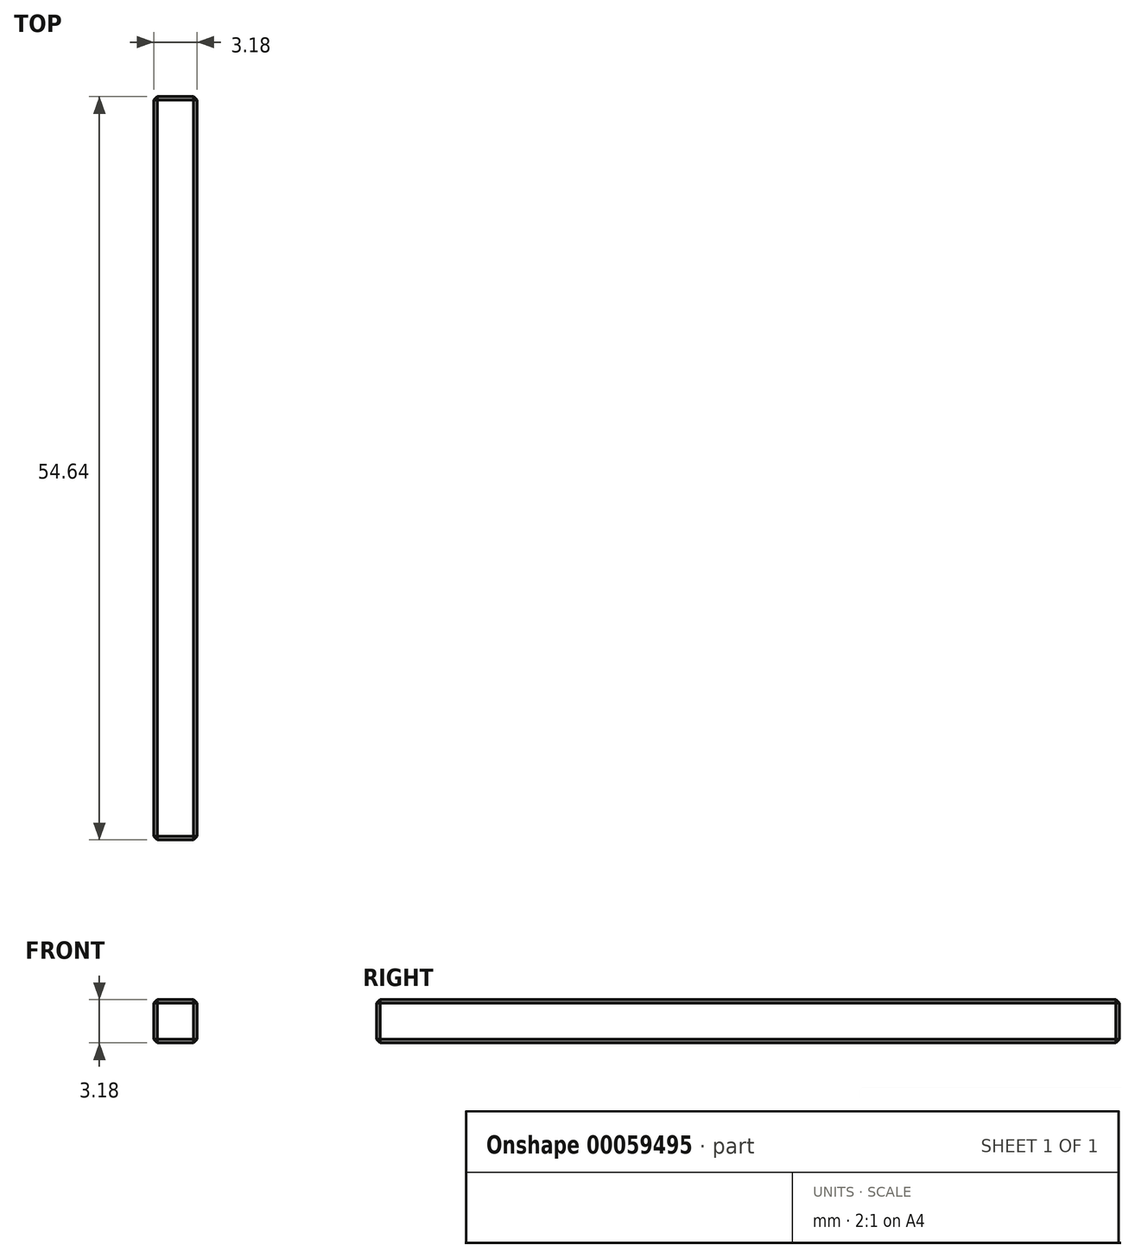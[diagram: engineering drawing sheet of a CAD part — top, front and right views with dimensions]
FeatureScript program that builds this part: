
annotation { "Feature Type Name" : "Feature", "Feature Type Description" : "" }
export const myFeature = defineFeature(function(context is Context, id is Id, definition is map)
    precondition{}
    {
        {
            var Q0;
            Q0=qCreatedBy(makeId("Front.planeOp"),FACE);
            var sketch = newSketch(context, id + "F0", { "sketchPlane" : qUnion([Q0])});
            skLineSegment(sketch, "E0.rect.bottom", {"start": v(1.59, 1.59) * mm, "end": v(-1.59, 1.59) * mm});
            skLineSegment(sketch, "E0.rect.top", {"start": v(1.59, -1.59) * mm, "end": v(-1.59, -1.59) * mm});
            skLineSegment(sketch, "E0.rect.left", {"start": v(1.59, 1.59) * mm, "end": v(1.59, -1.59) * mm});
            skLineSegment(sketch, "E0.rect.right", {"start": v(-1.59, 1.59) * mm, "end": v(-1.59, -1.59) * mm});
            skPoint(sketch, "E0.rect.middle", {"position": v(0, 0) * mm});
            skSolve(sketch);
        }
        {
            var Q0;
            Q0 = qSketchRegion(id + "F0", true);
            extrude(context, id + "F1", {"entities" : qUnion([Q0]), "oppositeDirection" : true, "depth" : 54.64 * mm});
        }
        {
            var Q0;
            Q0=makeQuery(id+"F1.opExtrude","CAP_EDGE",EDGE,{"disambiguationData":[OSD([sQuery(id+"F0.wireOp",EDGE,"E0.rect.bottom")])],"isStart":true});
            var Q1;
            Q1=makeQuery(id+"F1.opExtrude","CAP_EDGE",EDGE,{"disambiguationData":[OSD([sQuery(id+"F0.wireOp",EDGE,"E0.rect.left")])],"isStart":true});
            var Q2;
            Q2=makeQuery(id+"F1.opExtrude","CAP_EDGE",EDGE,{"disambiguationData":[OSD([sQuery(id+"F0.wireOp",EDGE,"E0.rect.top")])],"isStart":true});
            var Q3;
            Q3=makeQuery(id+"F1.opExtrude","CAP_EDGE",EDGE,{"disambiguationData":[OSD([sQuery(id+"F0.wireOp",EDGE,"E0.rect.right")])],"isStart":true});
            var Q4;
            Q4=makeQuery(id+"F1.opExtrude","SWEPT_EDGE",EDGE,{"disambiguationData":[OSD([sQuery(id+"F0.wireOp",EDGE,"E0.rect.bottom"),sQuery(id+"F0.wireOp",EDGE,"E0.rect.left")])]});
            var Q5;
            Q5=makeQuery(id+"F1.opExtrude","SWEPT_EDGE",EDGE,{"disambiguationData":[OSD([sQuery(id+"F0.wireOp",EDGE,"E0.rect.top"),sQuery(id+"F0.wireOp",EDGE,"E0.rect.left")])]});
            var Q6;
            Q6=makeQuery(id+"F1.opExtrude","SWEPT_EDGE",EDGE,{"disambiguationData":[OSD([sQuery(id+"F0.wireOp",EDGE,"E0.rect.bottom"),sQuery(id+"F0.wireOp",EDGE,"E0.rect.right")])]});
            var Q7;
            Q7=makeQuery(id+"F1.opExtrude","SWEPT_EDGE",EDGE,{"disambiguationData":[OSD([sQuery(id+"F0.wireOp",EDGE,"E0.rect.top"),sQuery(id+"F0.wireOp",EDGE,"E0.rect.right")])]});
            var Q8;
            Q8=makeQuery(id+"F1.opExtrude","CAP_EDGE",EDGE,{"disambiguationData":[OSD([sQuery(id+"F0.wireOp",EDGE,"E0.rect.top")])],"isStart":false});
            var Q9;
            Q9=makeQuery(id+"F1.opExtrude","CAP_EDGE",EDGE,{"disambiguationData":[OSD([sQuery(id+"F0.wireOp",EDGE,"E0.rect.bottom")])],"isStart":false});
            var Q10;
            Q10=makeQuery(id+"F1.opExtrude","CAP_EDGE",EDGE,{"disambiguationData":[OSD([sQuery(id+"F0.wireOp",EDGE,"E0.rect.left")])],"isStart":false});
            var Q11;
            Q11=makeQuery(id+"F1.opExtrude","CAP_EDGE",EDGE,{"disambiguationData":[OSD([sQuery(id+"F0.wireOp",EDGE,"E0.rect.right")])],"isStart":false});
            chamfer(context, id + "F2", {"entities" : qUnion([Q0, Q1, Q2, Q3, Q4, Q5, Q6, Q7, Q8, Q9, Q10, Q11]), "width" : 0.25 * mm, "tangentPropagation" : true});
        }
    });
